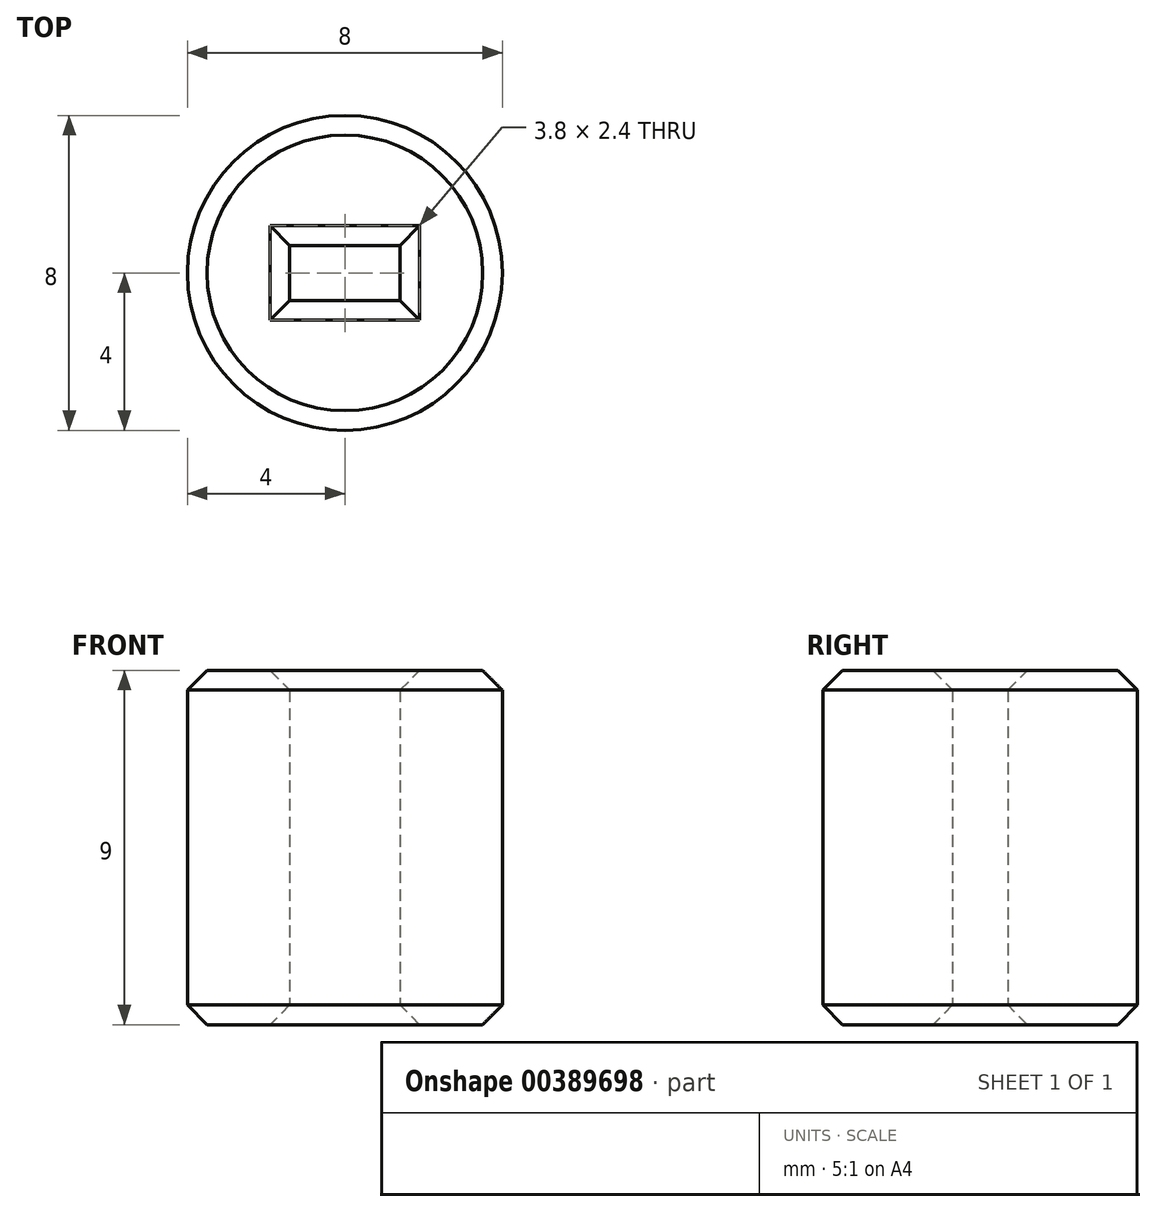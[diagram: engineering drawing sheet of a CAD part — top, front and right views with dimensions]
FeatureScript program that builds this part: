
annotation { "Feature Type Name" : "Feature", "Feature Type Description" : "" }
export const myFeature = defineFeature(function(context is Context, id is Id, definition is map)
    precondition{}
    {
        {
            var Q0;
            Q0=qCreatedBy(makeId("Top.planeOp"),FACE);
            var sketch = newSketch(context, id + "F0", { "sketchPlane" : qUnion([Q0])});
            skLineSegment(sketch, "E0.bottom", {"start": v(-1.4, 0.7) * mm, "end": v(1.4, 0.7) * mm});
            skLineSegment(sketch, "E0.top", {"start": v(-1.4, -0.7) * mm, "end": v(1.4, -0.7) * mm});
            skLineSegment(sketch, "E0.left", {"start": v(-1.4, 0.7) * mm, "end": v(-1.4, -0.7) * mm});
            skLineSegment(sketch, "E0.right", {"start": v(1.4, 0.7) * mm, "end": v(1.4, -0.7) * mm});
            skPoint(sketch, "E0.middle", {"position": v(0, 0) * mm});
            skCircle(sketch, "E1", {"center": v(0, 0) * mm, "radius": 4 * mm});
            skSolve(sketch);
        }
        {
            var Q0;
            Q0 = qSketchRegion(id + "F0", true);
            extrude(context, id + "F1", {"entities" : qUnion([Q0]), "depth" : 9 * mm});
        }
        {
            var Q0;
            Q0=makeQuery(id+"F1.opExtrude","CAP_EDGE",EDGE,{"disambiguationData":[OSD([sQuery(id+"F0.wireOp",EDGE,"E1")])],"isStart":false});
            var Q1;
            Q1=makeQuery(id+"F1.opExtrude","CAP_EDGE",EDGE,{"disambiguationData":[OSD([sQuery(id+"F0.wireOp",EDGE,"E1")])],"isStart":true});
            var Q2;
            Q2=makeQuery(id+"F1.opExtrude","CAP_EDGE",EDGE,{"disambiguationData":[OSD([sQuery(id+"F0.wireOp",EDGE,"E0.right")])],"isStart":true});
            var Q3;
            Q3=makeQuery(id+"F1.opExtrude","CAP_EDGE",EDGE,{"disambiguationData":[OSD([sQuery(id+"F0.wireOp",EDGE,"E0.bottom")])],"isStart":true});
            var Q4;
            Q4=makeQuery(id+"F1.opExtrude","CAP_EDGE",EDGE,{"disambiguationData":[OSD([sQuery(id+"F0.wireOp",EDGE,"E0.left")])],"isStart":true});
            var Q5;
            Q5=makeQuery(id+"F1.opExtrude","CAP_EDGE",EDGE,{"disambiguationData":[OSD([sQuery(id+"F0.wireOp",EDGE,"E0.top")])],"isStart":true});
            var Q6;
            Q6=makeQuery(id+"F1.opExtrude","CAP_EDGE",EDGE,{"disambiguationData":[OSD([sQuery(id+"F0.wireOp",EDGE,"E0.bottom")])],"isStart":false});
            var Q7;
            Q7=makeQuery(id+"F1.opExtrude","CAP_EDGE",EDGE,{"disambiguationData":[OSD([sQuery(id+"F0.wireOp",EDGE,"E0.right")])],"isStart":false});
            var Q8;
            Q8=makeQuery(id+"F1.opExtrude","CAP_EDGE",EDGE,{"disambiguationData":[OSD([sQuery(id+"F0.wireOp",EDGE,"E0.left")])],"isStart":false});
            var Q9;
            Q9=makeQuery(id+"F1.opExtrude","CAP_EDGE",EDGE,{"disambiguationData":[OSD([sQuery(id+"F0.wireOp",EDGE,"E0.top")])],"isStart":false});
            chamfer(context, id + "F2", {"entities" : qUnion([Q0, Q1, Q2, Q3, Q4, Q5, Q6, Q7, Q8, Q9]), "width" : .5 * mm, "tangentPropagation" : true});
        }
    });
